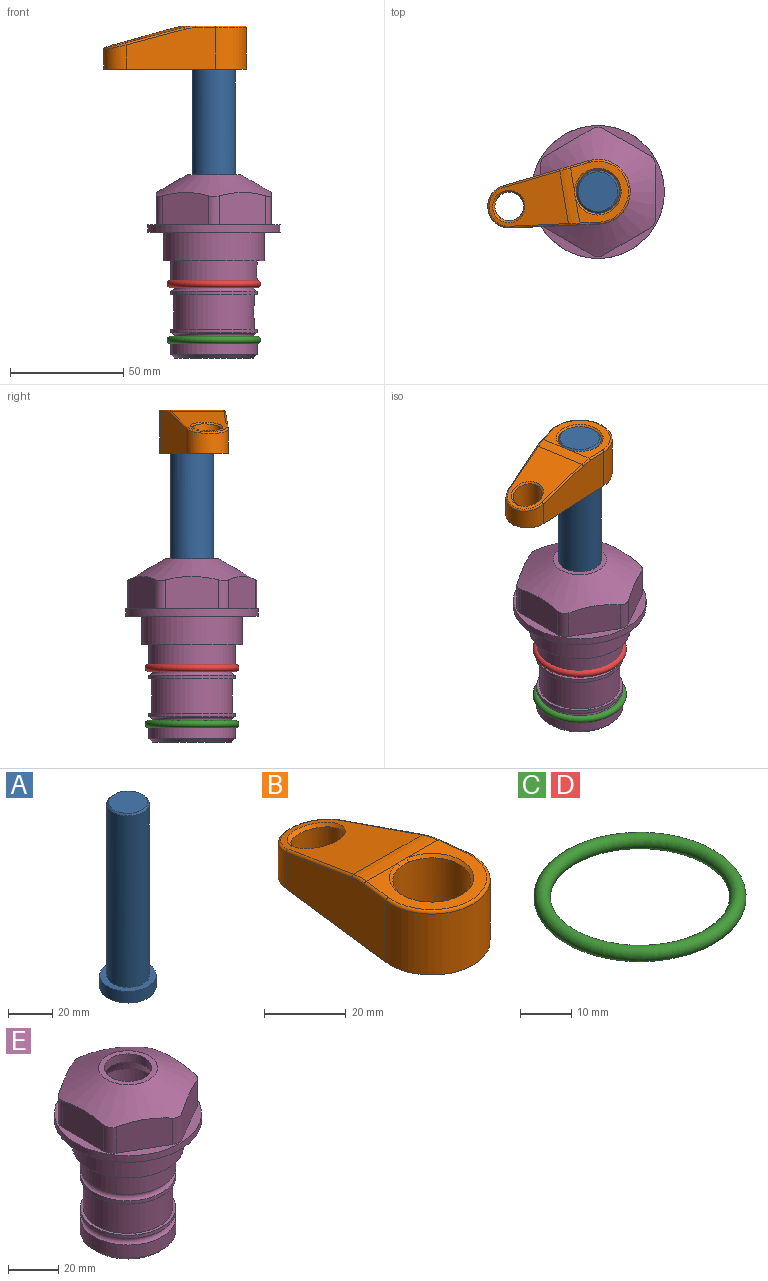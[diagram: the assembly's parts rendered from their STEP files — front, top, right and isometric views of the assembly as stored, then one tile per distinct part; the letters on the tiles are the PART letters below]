
ASSEMBLY  parts=5 mates=4
PART A: 6 faces, bbox 25.4x25.4x101.6 mm
  f0: plane 17.46x17.46mm, normal (0,0,1), area 239.5mm2, adj f5
  f1: plane 25.4x25.4mm, normal (0,0,-1), area 506.7mm2, adj f2
  f2: cylinder r=12.7mm len=25.4mm, axis (0,0,1), area 506.7mm2, adj f1,f3
  f3: plane 25.4x25.4mm, normal (0,0,1), area 221.7mm2, adj f2,f4
  f4: cylinder r=9.53mm len=94.46mm, axis (0,0,1), area 5653mm2, adj f3,f5
  f5: cone r=8.73mm half-angle=45deg, axis (0,0,-1), area 64.4mm2, adj f0,f4
PART B: 31 faces, bbox 31.7x65.5x19.8 mm
  f0: plane 39.12x18.26mm, normal (0.99,0.12,0), area 612.2mm2, adj f1,f4,f7,f11,f13,f15
  f1: cylinder r=9.53mm len=18.91mm, axis (0,0,-1), area 296.1mm2, adj f0,f2,f7,f17
  f2: plane 39.12x18.26mm, normal (-0.99,0.12,0), area 612.2mm2, adj f1,f4,f7,f12,f14,f16
  f3: cylinder r=6.35mm len=12.7mm, axis (0,0,-1), area 362.4mm2, adj f7,f18
  f4: cylinder r=14.29mm len=28.58mm, axis (0,0,-1), area 882.2mm2, adj f0,f2,f7,f10
  f5: cylinder r=9.53mm len=19.05mm, axis (0,0,-1), area 1092.6mm2, adj f7,f19,f20
  f6: plane 26.99x23.69mm, normal (0,0,1), area 216.2mm2, adj f9,f10,f11,f12,f19
  f7: plane 63.5x28.58mm, normal (0,0,-1), area 661.8mm2, adj f0,f1,f2,f3,f4,f5,f22,f23
  f8: plane 33.52x23.6mm, normal (0,0.26,0.97), area 486mm2, adj f9,f15,f16,f17,f18
  f9: cylinder r=19.05mm len=24.72mm, axis (1,0,0), area 120.4mm2, adj f6,f8,f13,f14,f20
  f10: torus R=13.49mm, axis (0,0,1), area 59mm2, adj f4,f6,f11,f12
  f11: cylinder r=0.79mm len=8.67mm, axis (0.12,-0.99,0), area 10.8mm2, adj f0,f6,f10,f13
  f12: cylinder r=0.79mm len=8.67mm, axis (0.12,0.99,0), area 10.8mm2, adj f2,f6,f10,f14
  f13: bspline ~4.95x1.42mm, area 6.1mm2, adj f0,f9,f11,f15
  f14: bspline ~4.95x1.42mm, area 6.1mm2, adj f2,f9,f12,f16
  f15: cylinder r=0.79mm len=25.95mm, axis (0.12,-0.96,0.26), area 32.9mm2, adj f0,f8,f13,f17
  f16: cylinder r=0.79mm len=25.95mm, axis (0.12,0.96,-0.26), area 32.9mm2, adj f2,f8,f14,f17
  f17: bspline ~18.91x8.38mm, area 30mm2, adj f1,f8,f15,f16
  f18: bspline ~14.29x14.29mm, area 48.3mm2, adj f3,f8
  f19: cone r=9.53mm half-angle=45deg, axis (0,0,1), area 66.5mm2, adj f5,f6,f20
  f20: bspline ~3.22x0.96mm, area 3.5mm2, adj f5,f9,f19
  f21: plane 2.75x2.72mm, normal (0,0,-1), area 2.9mm2, adj f23,f25,f28
  f22: plane 23.05x15.88mm, normal (-0.99,-0.12,0), area 323.6mm2, adj f7,f25,f26,f27,f28,f29
  f23: plane 23.05x15.88mm, normal (0.99,-0.12,0), area 323.6mm2, adj f7,f21,f25,f27,f28,f30
  f24: cylinder r=9.53mm len=10.69mm, axis (0,0,-1), area 114.7mm2, adj f7,f27,f29,f30
  f25: cylinder r=12.7mm len=20.59mm, axis (0,0,-1), area 381.1mm2, adj f7,f21,f22,f23,f26,f28
  f26: plane 2.75x2.72mm, normal (0,0,-1), area 2.9mm2, adj f22,f25,f28
  f27: plane 19.72x18.37mm, normal (0,-0.26,-0.97), area 291.8mm2, adj f22,f23,f24,f28,f29,f30
  f28: cylinder r=15.88mm len=19.92mm, axis (1,0,0), area 54.8mm2, adj f21,f22,f23,f25,f26,f27
  f29: cylinder r=1.59mm len=11mm, axis (0,0,-1), area 34.7mm2, adj f7,f22,f24,f27
  f30: cylinder r=1.59mm len=11mm, axis (0,0,-1), area 34.7mm2, adj f7,f23,f24,f27
PART C: 1 faces, bbox 44.7x44.7x3.2 mm
  f0: torus R=19.05mm, axis (0,0,1), area 1193.9mm2
PART D: same geometry as C
PART E: 36 faces, bbox 58.7x58.7x81 mm
  f0: cylinder r=17.78mm len=35.56mm, axis (0,0,1), area 1670.8mm2, adj f23,f24,f31
  f1: cylinder r=19.05mm len=38.1mm, axis (0,0,1), area 1191.9mm2, adj f26,f27,f30
  f2: plane 58.66x58.66mm, normal (0,0,-1), area 1150.6mm2, adj f3,f28
  f3: cylinder r=29.33mm len=58.66mm, axis (0,0,-1), area 585.1mm2, adj f2,f4
  f4: plane 58.66x58.66mm, normal (0,0,1), area 475.9mm2, adj f3,f5,f6,f7,f8,f9,f10,f11
  f5: plane 20.32x14.34mm, normal (-0.5,0.87,0), area 324.4mm2, adj f4,f15,f16,f17
  f6: plane 20.32x14.34mm, normal (0.5,0.87,0), area 324.4mm2, adj f4,f14,f15,f17
  f7: plane 23.48x14.34mm, normal (1,0,0), area 324.4mm2, adj f4,f13,f14,f17
  f8: plane 20.32x14.34mm, normal (0.5,-0.87,0), area 324.4mm2, adj f4,f12,f13,f17
  f9: plane 20.32x14.34mm, normal (-0.5,-0.87,0), area 324.4mm2, adj f4,f11,f12,f17
  f10: plane 23.48x14.34mm, normal (-1,0,0), area 324.4mm2, adj f4,f11,f16,f17
  f11: cylinder r=5.08mm len=12.85mm, axis (0,0,-1), area 67.2mm2, adj f4,f9,f10,f17
  f12: cylinder r=5.08mm len=12.85mm, axis (0,0,-1), area 67.2mm2, adj f4,f8,f9,f17
  f13: cylinder r=5.08mm len=12.85mm, axis (0,0,-1), area 67.2mm2, adj f4,f7,f8,f17
  f14: cylinder r=5.08mm len=12.85mm, axis (0,0,-1), area 67.2mm2, adj f4,f6,f7,f17
  f15: cylinder r=5.08mm len=12.85mm, axis (0,0,-1), area 67.2mm2, adj f4,f5,f6,f17
  f16: cylinder r=5.08mm len=12.85mm, axis (0,0,-1), area 67.2mm2, adj f4,f5,f10,f17
  f17: cone r=11.73mm half-angle=60deg, axis (0,0,-1), area 2071.8mm2, adj f5,f6,f7,f8,f9,f10,f11,f12
  f18: plane 23.46x23.46mm, normal (0,0,1), area 147.4mm2, adj f17,f35
  f19: plane 34.93x34.93mm, normal (0,0,-1), area 958mm2, adj f29
  f20: cylinder r=19.05mm len=38.1mm, axis (0,0,1), area 760.1mm2, adj f21,f29
  f21: torus R=19.05mm, axis (0,0,1), area 565.3mm2, adj f20,f22
  f22: cylinder r=19.05mm len=38.1mm, axis (0,0,1), area 190mm2, adj f21,f23
  f23: plane 38.1x38.1mm, normal (0,0,1), area 146.9mm2, adj f0,f22
  f24: plane 38.1x38.1mm, normal (0,0,-1), area 146.9mm2, adj f0,f25
  f25: cylinder r=19.05mm len=38.1mm, axis (0,0,1), area 190mm2, adj f24,f26
  f26: torus R=19.05mm, axis (0,0,1), area 565.3mm2, adj f1,f25
  f27: plane 44.45x44.45mm, normal (0,0,-1), area 411.7mm2, adj f1,f28
  f28: cylinder r=22.23mm len=44.45mm, axis (0,0,1), area 1773.5mm2, adj f2,f27
  f29: cone r=19.05mm half-angle=45deg, axis (0,0,1), area 257.5mm2, adj f19,f20
  f30: cylinder r=3.17mm len=6.75mm, axis (-1,0,0), area 128mm2, adj f1,f33
  f31: cylinder r=3.17mm len=6.35mm, axis (-1,0,0), area 102.5mm2, adj f0,f33
  f32: plane 25.4x25.4mm, normal (0,0,1), area 506.7mm2, adj f33
  f33: cylinder r=12.7mm len=66.42mm, axis (0,0,-1), area 5236.2mm2, adj f30,f31,f32,f34
  f34: cone r=9.53mm half-angle=30deg, axis (0,0,-1), area 443.4mm2, adj f33,f35
  f35: cylinder r=9.53mm len=19.05mm, axis (0,0,-1), area 240.9mm2, adj f18,f34
PLACE A rot(axis=(0,0,1),99.4deg) t=(0,0,27.55)mm
PLACE B rot(axis=(0,0,1),99.4deg) t=(0,0,27.55)mm
PLACE C t=(0,0,-23.18)mm
PLACE D t=(0,0,1.59)mm
PLACE E at identity fixed
MATE fastened E.f0 <-> C.f0  axis (0,0,1) through (0,0,-47.69)mm
MATE fastened B.f4 <-> A.f2  axis (0,0,1) through (0,0,91.05)mm
MATE fastened E.f0 <-> D.f0  axis (0,0,1) through (0,0,-22.92)mm
MATE cylindrical A.f2 <-> E.f0  axis (0,0,-1) through (0,0,-10.55)mm
